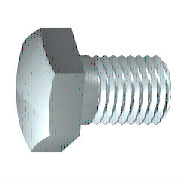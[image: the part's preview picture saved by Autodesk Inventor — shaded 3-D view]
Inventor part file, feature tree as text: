
AUTODESK INVENTOR PART (.ipt)
format: ipt  version: 2025.1 (Build 291241020, 241B)  size: 198,144 bytes
history: native  units: mm (DEFAULTED — no unit token found)
features: extrude x1, chamfer x1, plane x1
ambient origin geometry x7: Origin, YZ Plane, XZ Plane, X Axis, Y Axis, Z Axis, Center Point
bodies: Solid1 (feature_tree), Body (feature_tree)
feature tree (3):
  extrude  "Head"  Depth=35.0mm
  chamfer  "Chamfer1"  Distance=29.7mm
  plane  "Work Plane1"
